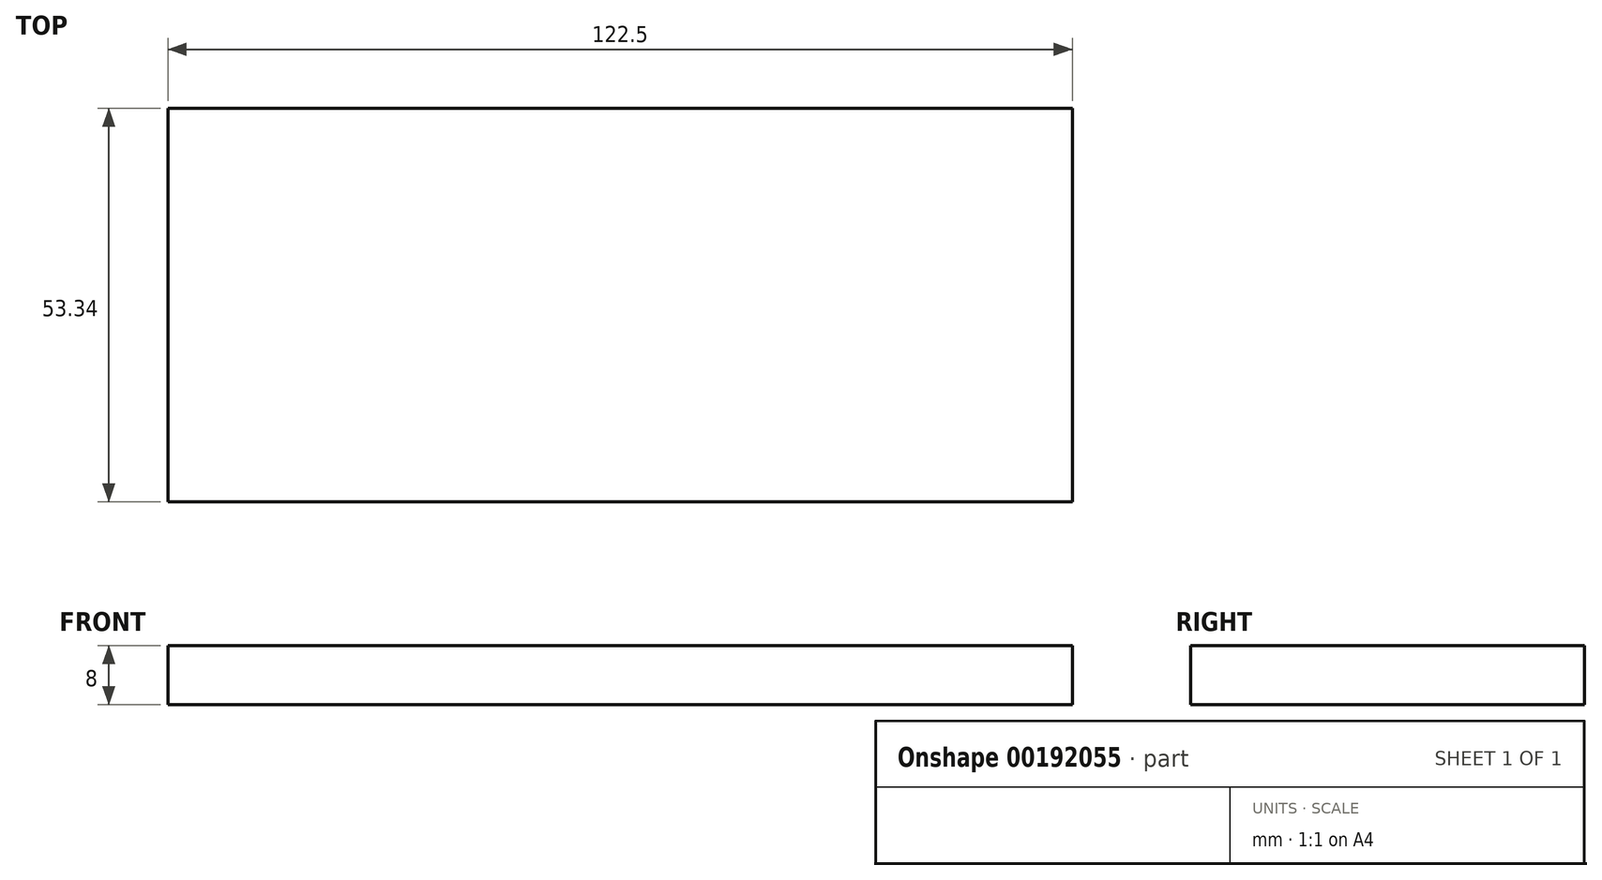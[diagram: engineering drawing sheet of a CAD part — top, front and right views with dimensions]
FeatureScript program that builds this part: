
annotation { "Feature Type Name" : "Feature", "Feature Type Description" : "" }
export const myFeature = defineFeature(function(context is Context, id is Id, definition is map)
    precondition{}
    {
        {
            var Q0;
            Q0=qCreatedBy(makeId("Top.planeOp"),FACE);
            var sketch = newSketch(context, id + "F0", { "sketchPlane" : qUnion([Q0])});
            skLineSegment(sketch, "E0.bottom", {"start": v(-61.25, 26.67) * mm, "end": v(61.25, 26.67) * mm});
            skLineSegment(sketch, "E0.top", {"start": v(-61.25, -26.67) * mm, "end": v(61.25, -26.67) * mm});
            skLineSegment(sketch, "E0.left", {"start": v(-61.25, 26.67) * mm, "end": v(-61.25, -26.67) * mm});
            skLineSegment(sketch, "E0.right", {"start": v(61.25, 26.67) * mm, "end": v(61.25, -26.67) * mm});
            skPoint(sketch, "E0.middle", {"position": v(0, 0) * mm});
            skSolve(sketch);
        }
        {
            var Q0;
            Q0=makeQuery(id+"F0.imprint","IMPRINT",FACE,{"disambiguationData":[TD([[makeQuery(id+"F0.imprint","IMPRINT",EDGE,{"derivedFrom":sQuery(id+"F0.wireOp",EDGE,"E0.bottom")}),-1.0]])]});
            extrude(context, id + "F1", {"entities" : qUnion([Q0]), "depth" : 8 * mm});
        }
    });
